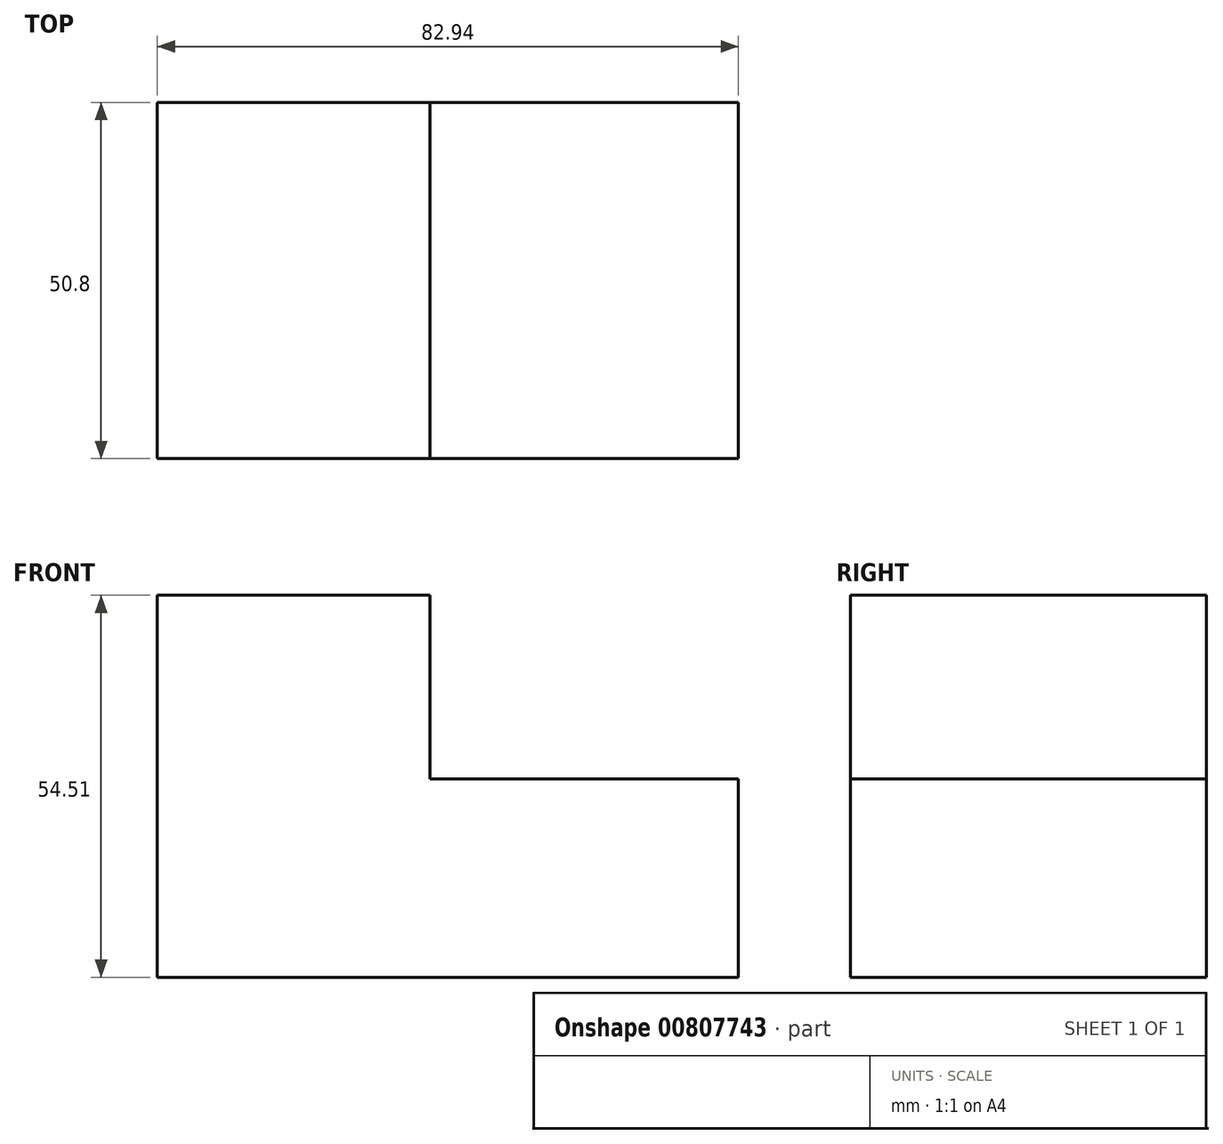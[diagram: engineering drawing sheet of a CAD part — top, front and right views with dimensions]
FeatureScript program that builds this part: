
annotation { "Feature Type Name" : "Feature", "Feature Type Description" : "" }
export const myFeature = defineFeature(function(context is Context, id is Id, definition is map)
    precondition{}
    {
        {
            var Q0;
            Q0=qCreatedBy(makeId("Front.planeOp"),FACE);
            var sketch = newSketch(context, id + "F0", { "sketchPlane" : qUnion([Q0])});
            skLineSegment(sketch, "E0", {"start": v(0, 0) * mm, "end": v(0, 26.19) * mm});
            skLineSegment(sketch, "E1", {"start": v(0, 26.19) * mm, "end": v(38.9, 26.19) * mm});
            skLineSegment(sketch, "E2", {"start": v(38.9, 26.19) * mm, "end": v(38.9, 0) * mm});
            skLineSegment(sketch, "E3", {"start": v(38.9, 0) * mm, "end": v(82.94, 0) * mm});
            skLineSegment(sketch, "E4", {"start": v(82.94, 0) * mm, "end": v(82.94, -28.32) * mm});
            skLineSegment(sketch, "E5", {"start": v(82.94, -28.32) * mm, "end": v(0, -28.32) * mm});
            skLineSegment(sketch, "E6", {"start": v(0, -28.32) * mm, "end": v(0, 26.19) * mm});
            skSolve(sketch);
        }
        {
            var Q0;
            {var subQ0=sQuery(id+"F0.wireOp",EDGE,"E1");Q0=makeQuery(id+"F0.imprint","IMPRINT",FACE,{"disambiguationData":[TD([[makeQuery(id+"F0.imprint","IMPRINT",EDGE,{"derivedFrom":subQ0}),-1.0]])]});}
            extrude(context, id + "F1", {"entities" : qUnion([Q0]), "depth" : 50.8 * mm, "offsetDistance" : 25.4 * mm});
        }
    });
